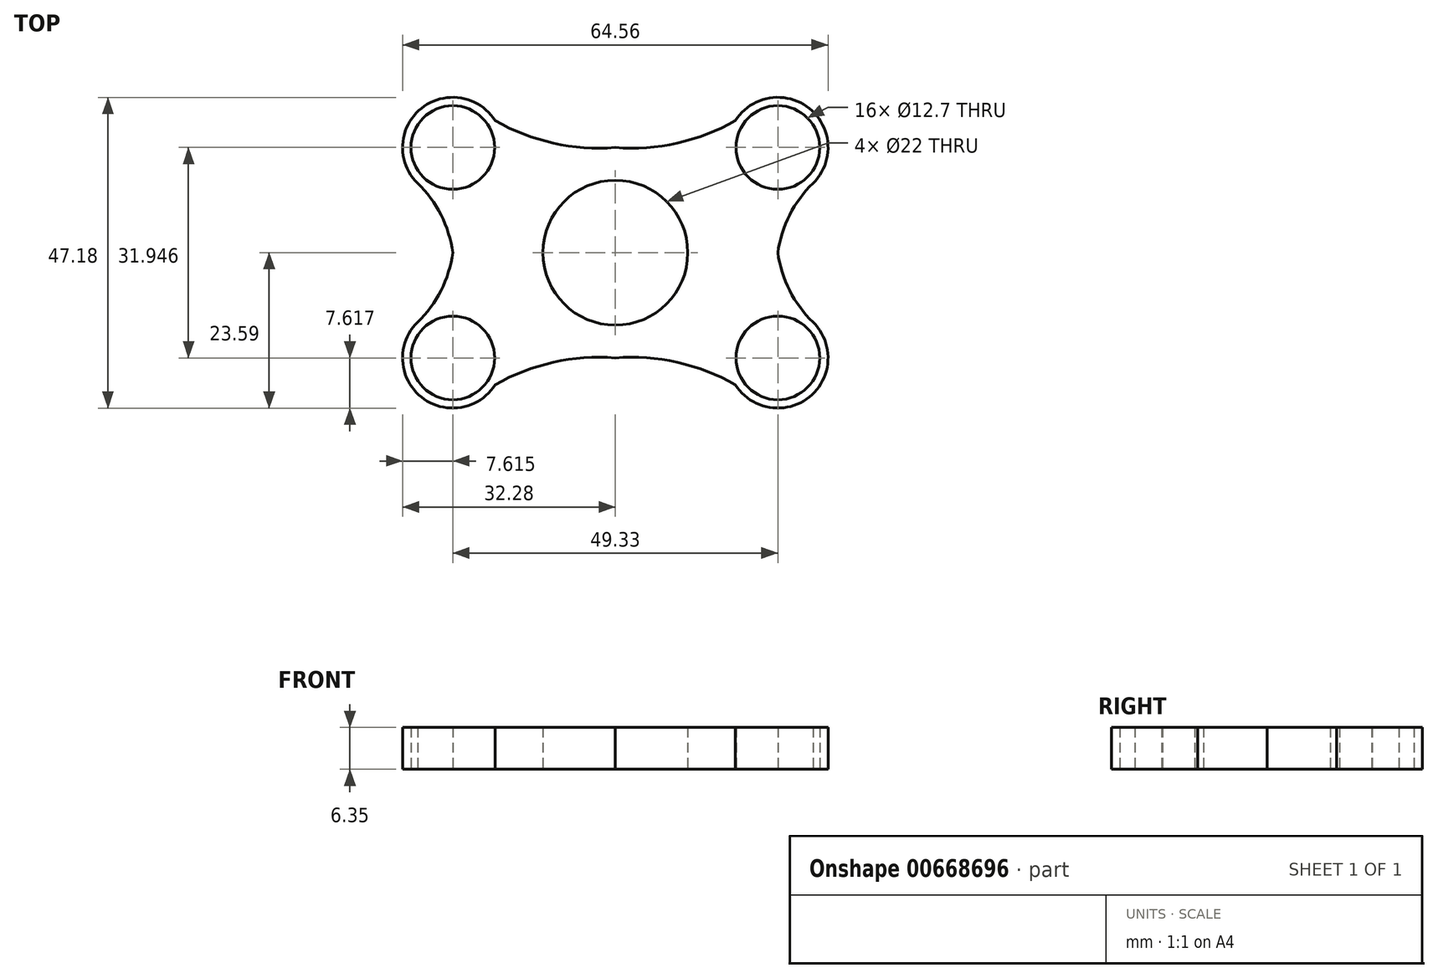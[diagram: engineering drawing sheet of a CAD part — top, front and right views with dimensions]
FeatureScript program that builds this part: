
annotation { "Feature Type Name" : "Feature", "Feature Type Description" : "" }
export const myFeature = defineFeature(function(context is Context, id is Id, definition is map)
    precondition{}
    {
        {
            var Q0;
            Q0=qCreatedBy(makeId("Top.planeOp"),FACE);
            var sketch = newSketch(context, id + "F0", { "sketchPlane" : qUnion([Q0])});
            skCircle(sketch, "E0", {"center": v(0, 0) * mm, "radius": 11 * mm});
            skLineSegment(sketch, "E1.bottom", {"start": v(-38.1, -25.4) * mm, "end": v(38.1, -25.4) * mm});
            skLineSegment(sketch, "E1.top", {"start": v(-38.1, 25.4) * mm, "end": v(38.1, 25.4) * mm});
            skLineSegment(sketch, "E1.left", {"start": v(-38.1, -25.4) * mm, "end": v(-38.1, 25.4) * mm});
            skLineSegment(sketch, "E1.right", {"start": v(38.1, -25.4) * mm, "end": v(38.1, 25.4) * mm});
            skLineSegment(sketch, "E2.bottom", {"start": v(-4.91, -15.97) * mm, "end": v(4.91, -15.97) * mm});
            skLineSegment(sketch, "E2.top", {"start": v(-4.91, 15.97) * mm, "end": v(4.91, 15.97) * mm});
            skCircle(sketch, "E3", {"center": v(-24.66, 15.97) * mm, "radius": 6.35 * mm});
            skCircle(sketch, "E4", {"center": v(24.66, 15.97) * mm, "radius": 6.35 * mm});
            skCircle(sketch, "E5", {"center": v(-24.66, -15.97) * mm, "radius": 6.35 * mm});
            skCircle(sketch, "E6", {"center": v(24.66, -15.97) * mm, "radius": 6.35 * mm});
            skArc(sketch, "E7", {"start": v(-18.22, 20.04) * mm, "mid": v(-29.5, 21.87) * mm, "end": v(-29.92, 10.46) * mm});
            skArc(sketch, "E8", {"start": v(29.92, 10.46) * mm, "mid": v(29.5, 21.87) * mm, "end": v(18.22, 20.04) * mm});
            skArc(sketch, "E9", {"start": v(18.22, -20.04) * mm, "mid": v(29.5, -21.87) * mm, "end": v(29.92, -10.46) * mm});
            skArc(sketch, "E10", {"start": v(-29.92, -10.46) * mm, "mid": v(-29.5, -21.87) * mm, "end": v(-18.22, -20.04) * mm});
            skArc(sketch, "E11", {"start": v(-18.22, 20.04) * mm, "mid": v(-9.42, 16.65) * mm, "end": v(0, 15.97) * mm});
            skArc(sketch, "E12.MirrorCS", {"start": v(18.22, 20.04) * mm, "mid": v(9.42, 16.65) * mm, "end": v(0, 15.97) * mm});
            skArc(sketch, "E13.MirrorCS", {"start": v(18.22, -20.04) * mm, "mid": v(9.42, -16.65) * mm, "end": v(0, -15.97) * mm});
            skArc(sketch, "E14.MirrorCS", {"start": v(-18.22, -20.04) * mm, "mid": v(-9.42, -16.65) * mm, "end": v(0, -15.97) * mm});
            skPoint(sketch, "E15.orphan", {"position": v(-17.04, 15.97) * mm});
            skPoint(sketch, "E16.orphan", {"position": v(17.04, 15.97) * mm});
            skArc(sketch, "E17", {"start": v(30.02, 10.55) * mm, "mid": v(26.45, 5.73) * mm, "end": v(24.66, 0) * mm});
            skArc(sketch, "E18.MirrorCS", {"start": v(30.02, -10.55) * mm, "mid": v(26.45, -5.73) * mm, "end": v(24.66, 0) * mm});
            skArc(sketch, "E19.MirrorCS", {"start": v(-30.02, 10.55) * mm, "mid": v(-26.45, 5.73) * mm, "end": v(-24.66, 0) * mm});
            skArc(sketch, "E20.MirrorCS", {"start": v(-30.02, -10.55) * mm, "mid": v(-26.45, -5.73) * mm, "end": v(-24.66, 0) * mm});
            skPoint(sketch, "E21.orphan", {"position": v(24.66, 8.35) * mm});
            skPoint(sketch, "E22.trimOffspring.start.orphan", {"position": v(24.66, -8.35) * mm});
            skSolve(sketch);
        }
        {
            var Q0;
            Q0=makeQuery(id+"F0.imprint","IMPRINT",FACE,{"disambiguationData":[TD([[makeQuery(id+"F0.imprint","IMPRINT",EDGE,{"derivedFrom":sQuery(id+"F0.wireOp",EDGE,"E0")}),-1.0]])]});
            extrude(context, id + "F1", {"entities" : qUnion([Q0]), "depth" : 6.35 * mm, "offsetDistance" : 25.4 * mm});
        }
    });
